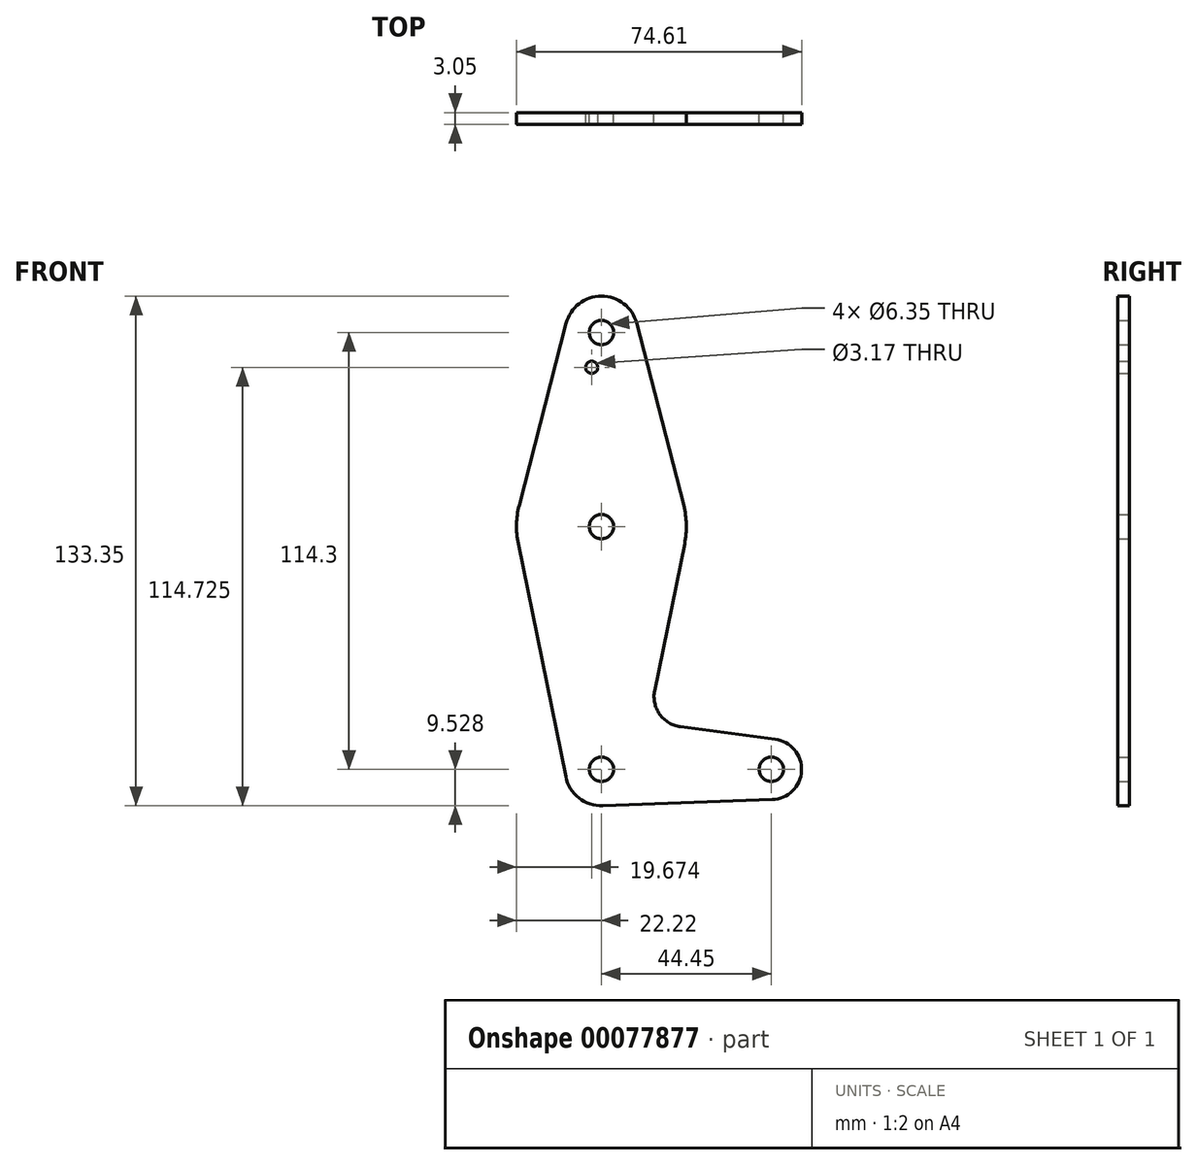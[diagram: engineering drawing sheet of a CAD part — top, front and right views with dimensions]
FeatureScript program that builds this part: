
annotation { "Feature Type Name" : "Feature", "Feature Type Description" : "" }
export const myFeature = defineFeature(function(context is Context, id is Id, definition is map)
    precondition{}
    {
        {
            var Q0;
            Q0=qCreatedBy(makeId("Front.planeOp"),FACE);
            var sketch = newSketch(context, id + "F0", { "sketchPlane" : qUnion([Q0])});
            skLineSegment(sketch, "E0", {"start": v(0, 52.88) * mm, "end": v(0, -61.42) * mm});
            skCircle(sketch, "E1", {"center": v(0, 52.88) * mm, "radius": 9.53 * mm});
            skCircle(sketch, "E2", {"center": v(0, 2.08) * mm, "radius": 22.23 * mm});
            skCircle(sketch, "E3", {"center": v(0, -61.42) * mm, "radius": 9.53 * mm});
            skCircle(sketch, "E4", {"center": v(44.45, -61.42) * mm, "radius": 7.94 * mm});
            skLineSegment(sketch, "E5", {"start": v(44.73, -69.35) * mm, "end": v(0, -70.95) * mm});
            skLineSegment(sketch, "E6", {"start": v(45.48, -53.55) * mm, "end": v(20.68, -50.31) * mm});
            skLineSegment(sketch, "E7", {"start": v(13.92, -40.84) * mm, "end": v(21.78, -2.37) * mm});
            skLineSegment(sketch, "E8", {"start": v(-9.33, -63.33) * mm, "end": v(-21.78, -2.37) * mm});
            skLineSegment(sketch, "E9", {"start": v(-9.22, 55.26) * mm, "end": v(-21.52, 7.63) * mm});
            skLineSegment(sketch, "E10", {"start": v(9.22, 55.26) * mm, "end": v(21.52, 7.63) * mm});
            skCircle(sketch, "E11", {"center": v(-2.55, 43.78) * mm, "radius": 1.59 * mm});
            skCircle(sketch, "E12", {"center": v(0, 52.88) * mm, "radius": 3.18 * mm});
            skCircle(sketch, "E13", {"center": v(0, 2.08) * mm, "radius": 3.18 * mm});
            skCircle(sketch, "E14", {"center": v(0, -61.42) * mm, "radius": 3.18 * mm});
            skCircle(sketch, "E15", {"center": v(44.45, -61.42) * mm, "radius": 3.18 * mm});
            skArc(sketch, "E16.filletArc", {"start": v(13.92, -40.84) * mm, "mid": v(15.24, -47.04) * mm, "end": v(20.68, -50.31) * mm});
            skSolve(sketch);
        }
        {
            var Q0;
            Q0 = qSketchRegion(id + "F0", true);
            extrude(context, id + "F1", {"entities" : qUnion([Q0]), "depth" : 3.05 * mm});
        }
    });
